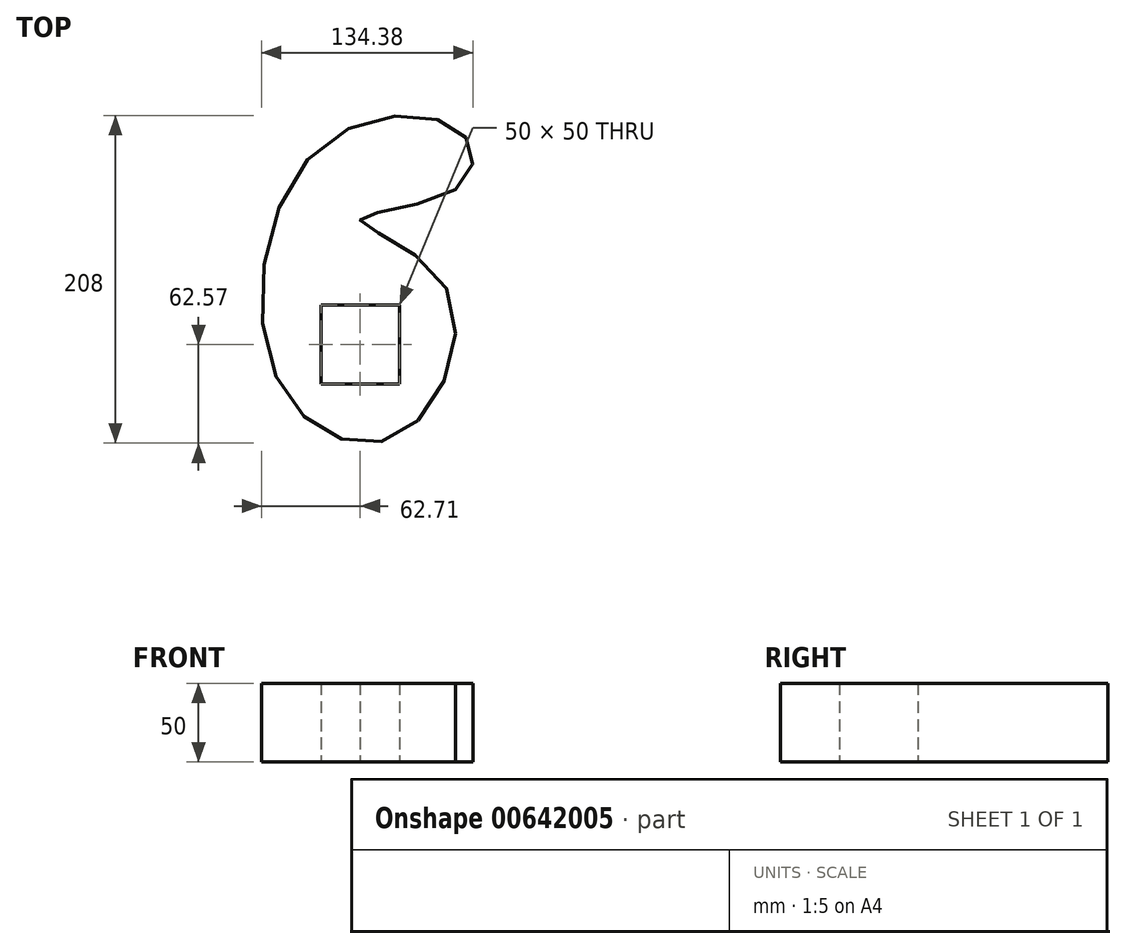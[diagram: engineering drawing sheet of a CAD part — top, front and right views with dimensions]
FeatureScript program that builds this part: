
annotation { "Feature Type Name" : "Feature", "Feature Type Description" : "" }
export const myFeature = defineFeature(function(context is Context, id is Id, definition is map)
    precondition{}
    {
        {
            var Q0;
            Q0=qCreatedBy(makeId("Top.planeOp"),FACE);
            var sketch = newSketch(context, id + "F0", { "sketchPlane" : qUnion([Q0])});
            skLineSegment(sketch, "E0.bottom", {"start": v(25, -25) * mm, "end": v(-25, -25) * mm});
            skLineSegment(sketch, "E0.top", {"start": v(25, 25) * mm, "end": v(-25, 25) * mm});
            skLineSegment(sketch, "E0.left", {"start": v(25, -25) * mm, "end": v(25, 25) * mm});
            skLineSegment(sketch, "E0.right", {"start": v(-25, -25) * mm, "end": v(-25, 25) * mm});
            skPoint(sketch, "E0.middle", {"position": v(0, 0) * mm});
            skPoint(sketch, "E1.1.internal.snap0", {"position": v(0, 25) * mm});
            skPoint(sketch, "E1.4.internal.snap0", {"position": v(0, -25) * mm});
            skFitSpline(sketch, "E1", {"points": [v(60.38, 98.57) * mm, v(0, 79.66) * mm, v(53.1, 38.56) * mm, v(25, -57.1) * mm, v(-51.29, -25) * mm, v(-25, 125.85) * mm, v(64.74, 134.22) * mm, v(60.38, 98.57) * mm]});
            skSolve(sketch);
        }
        {
            var Q0;
            Q0 = qSketchRegion(id + "F0", true);
            extrude(context, id + "F1", {"entities" : qUnion([Q0]), "depth" : 50 * mm, "offsetDistance" : 25 * mm});
        }
        {
            var Q0;
            Q0 = qSketchRegion(id + "F0", true);
            extrude(context, id + "F2", {"entities" : qUnion([Q0]), "operationType" : NewBodyOperationType.ADD, "depth" : 25 * mm, "offsetDistance" : 25 * mm});
        }
    });
